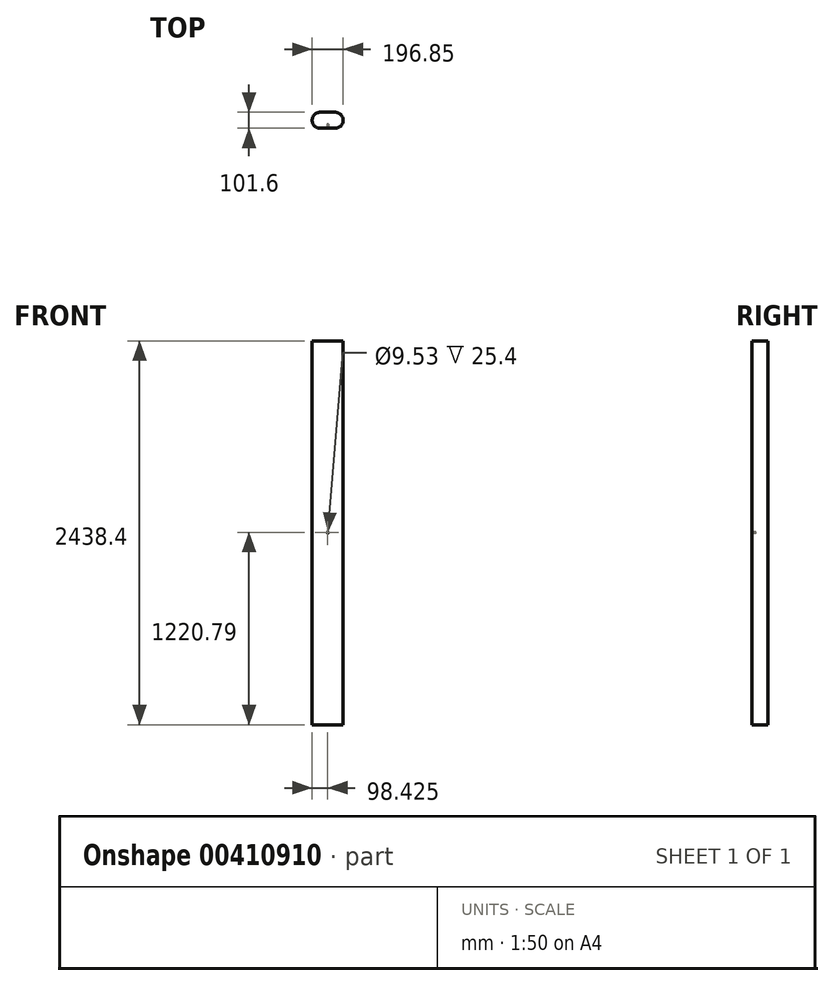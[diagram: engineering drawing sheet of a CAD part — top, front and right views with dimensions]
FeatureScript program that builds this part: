
annotation { "Feature Type Name" : "Feature", "Feature Type Description" : "" }
export const myFeature = defineFeature(function(context is Context, id is Id, definition is map)
    precondition{}
    {
        {
            var Q0;
            Q0=qCreatedBy(makeId("Top.planeOp"),FACE);
            var sketch = newSketch(context, id + "F0", { "sketchPlane" : qUnion([Q0])});
            skLineSegment(sketch, "E0", {"start": v(0, 0) * mm, "end": v(-196.85, 0) * mm});
            skLineSegment(sketch, "E1", {"start": v(-196.85, 0) * mm, "end": v(-196.85, 101.6) * mm});
            skLineSegment(sketch, "E2", {"start": v(-196.85, 101.6) * mm, "end": v(0, 101.6) * mm});
            skLineSegment(sketch, "E3", {"start": v(0, 101.6) * mm, "end": v(0, 0) * mm});
            skSolve(sketch);
        }
        {
            var Q0;
            Q0=makeQuery(id+"F0.imprint","IMPRINT",FACE,{"disambiguationData":[TD([[makeQuery(id+"F0.imprint","IMPRINT",EDGE,{"derivedFrom":sQuery(id+"F0.wireOp",EDGE,"E0")}),-1.0]])]});
            extrude(context, id + "F1", {"entities" : qUnion([Q0]), "depth" : 2438.4 * mm});
        }
        {
            var Q0;
            Q0=makeQuery(id+"F1.opExtrude","SWEPT_EDGE",EDGE,{"disambiguationData":[OSD([sQuery(id+"F0.wireOp",EDGE,"E0"),sQuery(id+"F0.wireOp",EDGE,"E3")])]});
            var Q1;
            Q1=makeQuery(id+"F1.opExtrude","SWEPT_EDGE",EDGE,{"disambiguationData":[OSD([sQuery(id+"F0.wireOp",EDGE,"E0"),sQuery(id+"F0.wireOp",EDGE,"E1")])]});
            var Q2;
            Q2=makeQuery(id+"F1.opExtrude","SWEPT_EDGE",EDGE,{"disambiguationData":[OSD([sQuery(id+"F0.wireOp",EDGE,"E1"),sQuery(id+"F0.wireOp",EDGE,"E2")])]});
            var Q3;
            Q3=makeQuery(id+"F1.opExtrude","SWEPT_EDGE",EDGE,{"disambiguationData":[OSD([sQuery(id+"F0.wireOp",EDGE,"E2"),sQuery(id+"F0.wireOp",EDGE,"E3")])]});
            fillet(context, id + "F2", {"entities" : qUnion([Q0, Q1, Q2, Q3]), "radius" : 50.8 * mm, "tangentPropagation" : true, "allowEdgeOverflow" : false});
        }
        {
            var Q0;
            Q0=makeQuery(id+"F1.opExtrude","SWEPT_FACE",FACE,{"disambiguationData":[OSD([sQuery(id+"F0.wireOp",EDGE,"E0")])]});
            var sketch = newSketch(context, id + "F3", { "sketchPlane" : qUnion([Q0])});
            skCircle(sketch, "E4", {"center": v(-98.43, 1220.79) * mm, "radius": 4.76 * mm});
            skSolve(sketch);
        }
        {
            var Q0;
            Q0 = qSketchRegion(id + "F3", true);
            extrude(context, id + "F4", {"entities" : qUnion([Q0]), "operationType" : NewBodyOperationType.REMOVE, "oppositeDirection" : true, "depth" : 25.4 * mm});
        }
        {
            var Q0;
            Q0=makeQuery(id+"F3.imprint","IMPRINT",FACE,{"disambiguationData":[TD([[makeQuery(id+"F3.imprint","IMPRINT",EDGE,{"derivedFrom":sQuery(id+"F3.wireOp",EDGE,"E4")}),1.0]])]});
            extrude(context, id + "F5", {"entities" : qUnion([Q0]), "operationType" : NewBodyOperationType.REMOVE, "oppositeDirection" : true, "depth" : 25.4 * mm});
        }
    });
